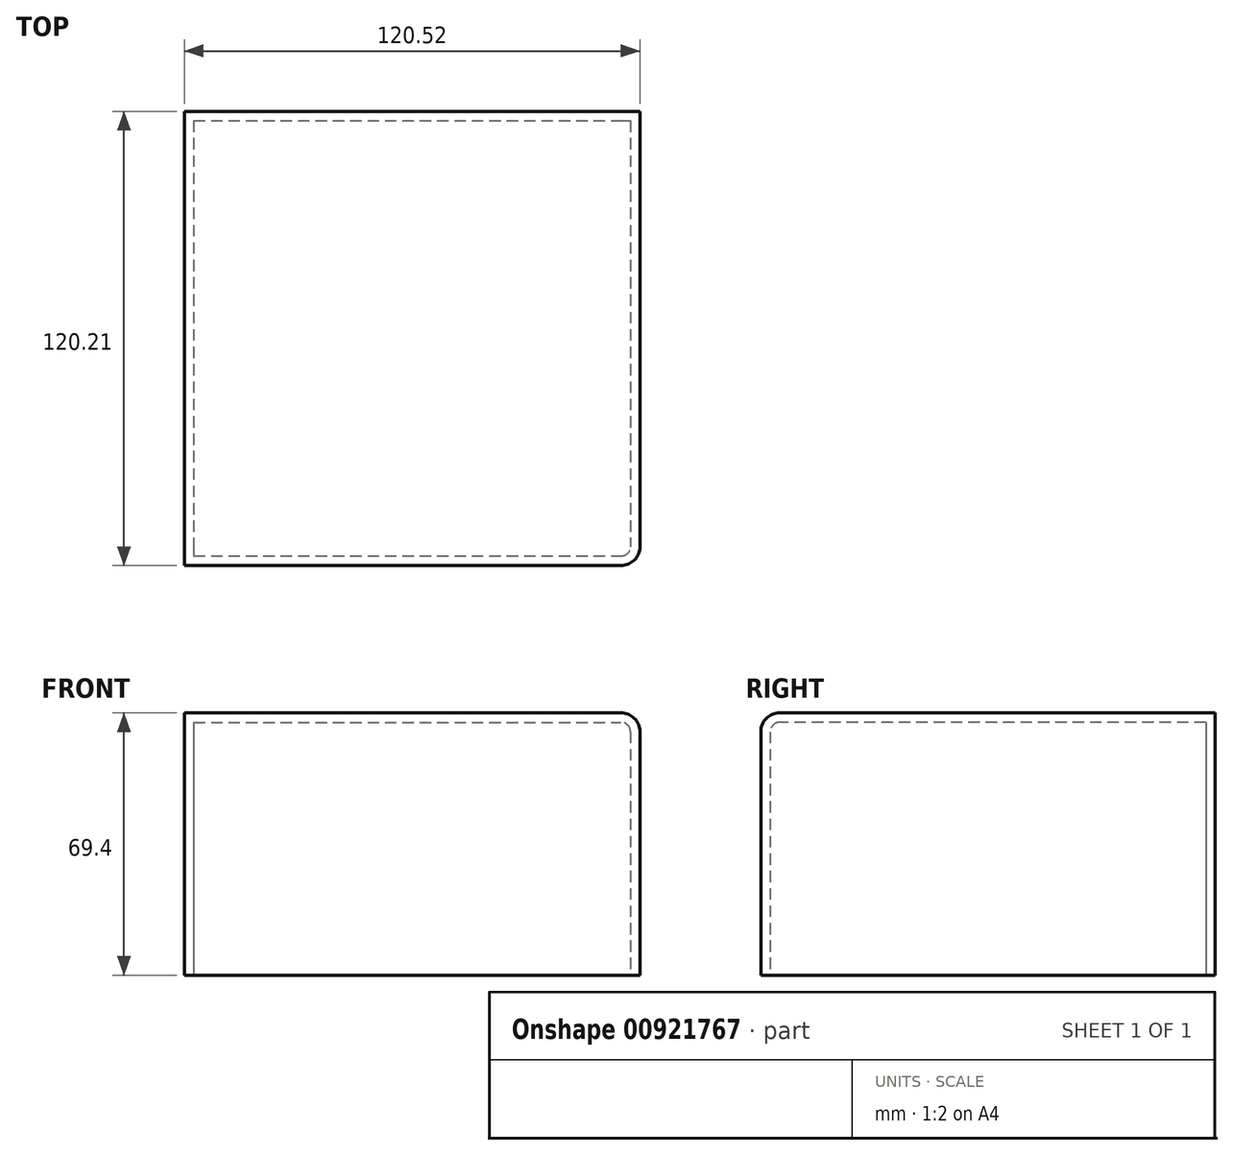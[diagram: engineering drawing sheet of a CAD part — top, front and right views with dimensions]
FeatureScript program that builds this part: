
annotation { "Feature Type Name" : "Feature", "Feature Type Description" : "" }
export const myFeature = defineFeature(function(context is Context, id is Id, definition is map)
    precondition{}
    {
        {
            var Q0;
            Q0=qCreatedBy(makeId("Top.planeOp"),FACE);
            var sketch = newSketch(context, id + "F0", { "sketchPlane" : qUnion([Q0])});
            skLineSegment(sketch, "E0.bottom", {"start": v(-52.25, 55.1) * mm, "end": v(68.27, 55.1) * mm});
            skLineSegment(sketch, "E0.top", {"start": v(-52.25, -65.1) * mm, "end": v(68.27, -65.1) * mm});
            skLineSegment(sketch, "E0.left", {"start": v(-52.25, 55.1) * mm, "end": v(-52.25, -65.1) * mm});
            skLineSegment(sketch, "E0.right", {"start": v(68.27, 55.1) * mm, "end": v(68.27, -65.1) * mm});
            skSolve(sketch);
        }
        {
            var Q0;
            Q0=makeQuery(id+"F0.imprint","IMPRINT",FACE,{"disambiguationData":[TD([[makeQuery(id+"F0.imprint","IMPRINT",EDGE,{"derivedFrom":sQuery(id+"F0.wireOp",EDGE,"E0.bottom")}),-1.0]])]});
            extrude(context, id + "F1", {"entities" : qUnion([Q0]), "depth" : 69.4 * mm, "offsetDistance" : 25 * mm});
        }
        {
            var Q0;
            Q0=makeQuery(id+"F1.opExtrude","CAP_EDGE",EDGE,{"disambiguationData":[OSD([sQuery(id+"F0.wireOp",EDGE,"E0.top")])],"isStart":false});
            var Q1;
            Q1=makeQuery(id+"F1.opExtrude","CAP_EDGE",EDGE,{"disambiguationData":[OSD([sQuery(id+"F0.wireOp",EDGE,"E0.right")])],"isStart":false});
            var Q2;
            Q2=makeQuery(id+"F1.opExtrude","SWEPT_EDGE",EDGE,{"disambiguationData":[OSD([sQuery(id+"F0.wireOp",EDGE,"E0.top"),sQuery(id+"F0.wireOp",EDGE,"E0.right")])]});
            fillet(context, id + "F2", {"entities" : qUnion([Q0, Q1, Q2]), "radius" : 5 * mm, "tangentPropagation" : true, "allowEdgeOverflow" : false});
        }
        {
            var Q0;
            Q0=makeQuery(id+"F1.opExtrude","CAP_FACE",FACE,{"disambiguationData":[OSD([sQuery(id+"F0.wireOp",EDGE,"E0.bottom"),sQuery(id+"F0.wireOp",EDGE,"E0.top"),sQuery(id+"F0.wireOp",EDGE,"E0.left"),sQuery(id+"F0.wireOp",EDGE,"E0.right")])],"isStart":true});
            shell(context, id + "F3", {"entities" : qUnion([Q0]), "thickness" : 2.5 * mm});
        }
    });
